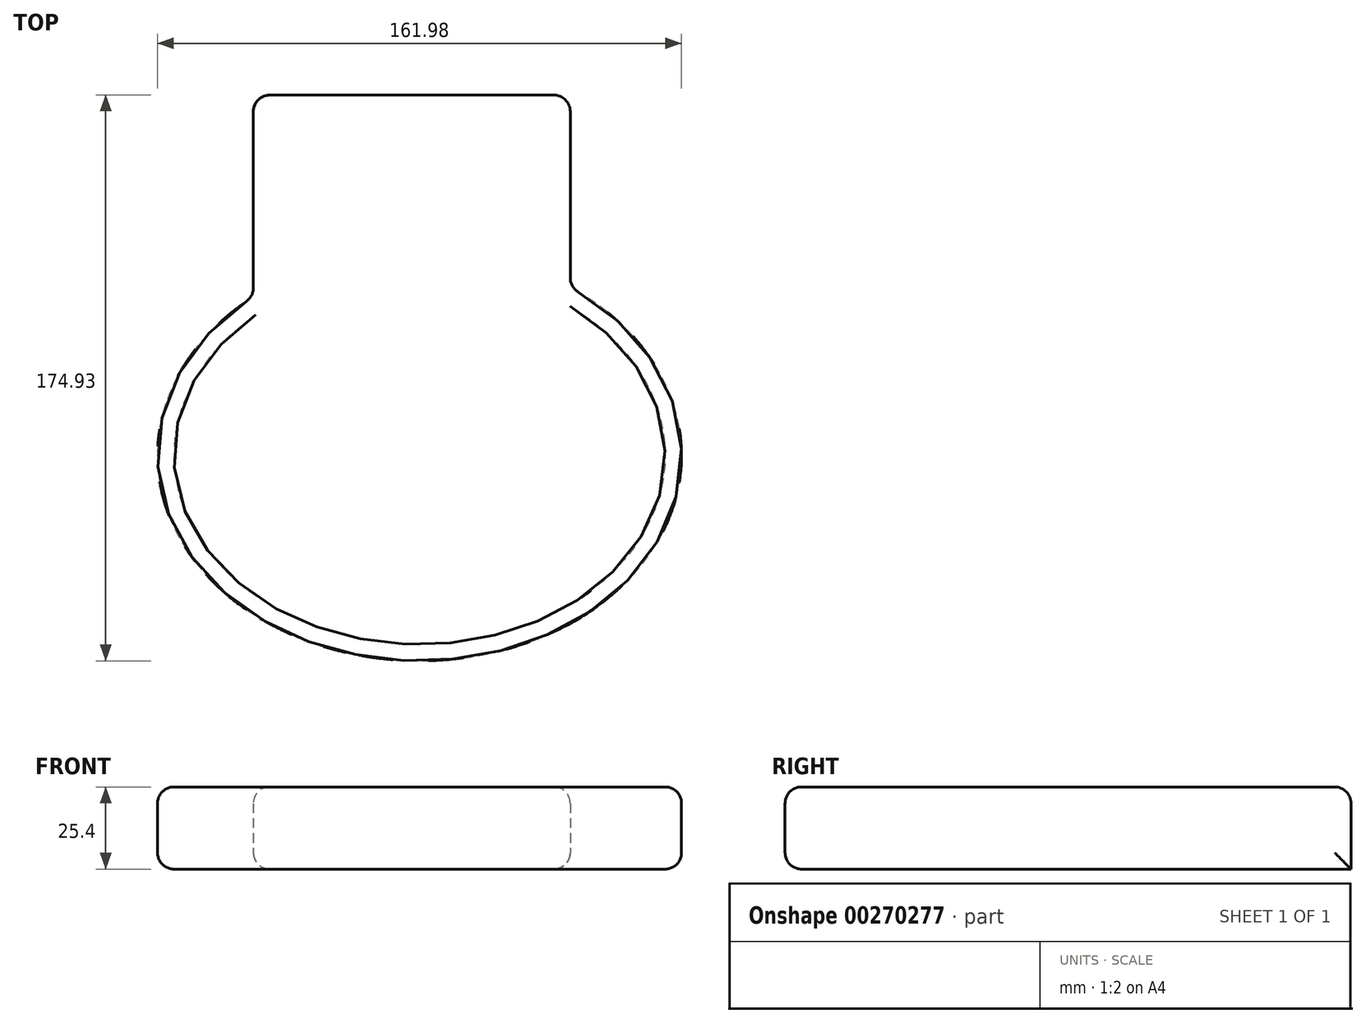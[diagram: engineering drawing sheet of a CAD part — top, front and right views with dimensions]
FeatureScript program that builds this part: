
annotation { "Feature Type Name" : "Feature", "Feature Type Description" : "" }
export const myFeature = defineFeature(function(context is Context, id is Id, definition is map)
    precondition{}
    {
        {
            var Q0;
            Q0=qCreatedBy(makeId("Top.planeOp"),FACE);
            var sketch = newSketch(context, id + "F0", { "sketchPlane" : qUnion([Q0])});
            skEllipse(sketch, "E0", {"center": v(0, 0) * mm, "majorRadius": 63.5 * mm, "minorRadius": 81 * mm, "majorAxis": v(0, 1)});
            skLineSegment(sketch, "E1", {"start": v(-51.38, 49.09) * mm, "end": v(-51.38, 111.43) * mm});
            skLineSegment(sketch, "E2", {"start": v(-51.38, 111.43) * mm, "end": v(46.59, 111.43) * mm});
            skLineSegment(sketch, "E3", {"start": v(46.59, 111.43) * mm, "end": v(46.59, 51.94) * mm});
            skSolve(sketch);
        }
        {
            var Q0;
            Q0 = qSketchRegion(id + "F0", true);
            var Q1;
            {var subQ0=sQuery(id+"F0.wireOp",EDGE,"E1");Q1=makeQuery(id+"F0.imprint","IMPRINT",FACE,{"disambiguationData":[TD([[makeQuery(id+"F0.imprint","IMPRINT",EDGE,{"derivedFrom":subQ0}),-1.0]])]});}
            extrude(context, id + "F1", {"entities" : qUnion([Q0, Q1]), "depth" : 25.4 * mm});
        }
        {
            var Q0;
            Q0=makeQuery(id+"F1.opExtrude","CAP_EDGE",EDGE,{"disambiguationData":[OSD([sQuery(id+"F0.wireOp",EDGE,"E0")])],"isStart":true});
            var Q1;
            Q1=makeQuery(id+"F1.opExtrude","CAP_EDGE",EDGE,{"disambiguationData":[OSD([sQuery(id+"F0.wireOp",EDGE,"E0")])],"isStart":false});
            var Q2;
            Q2=makeQuery(id+"F1.opExtrude","CAP_EDGE",EDGE,{"disambiguationData":[OSD([sQuery(id+"F0.wireOp",EDGE,"E3")])],"isStart":true});
            var Q3;
            Q3=makeQuery(id+"F1.opExtrude","CAP_EDGE",EDGE,{"disambiguationData":[OSD([sQuery(id+"F0.wireOp",EDGE,"E2")])],"isStart":false});
            var Q4;
            Q4=makeQuery(id+"F1.opExtrude","SWEPT_EDGE",EDGE,{"disambiguationData":[OSD([sQuery(id+"F0.wireOp",EDGE,"E2"),sQuery(id+"F0.wireOp",EDGE,"E3")])]});
            var Q5;
            Q5=makeQuery(id+"F1.opExtrude","CAP_EDGE",EDGE,{"disambiguationData":[OSD([sQuery(id+"F0.wireOp",EDGE,"E1")])],"isStart":false});
            var Q6;
            Q6=makeQuery(id+"F1.opExtrude","CAP_EDGE",EDGE,{"disambiguationData":[OSD([sQuery(id+"F0.wireOp",EDGE,"E3")])],"isStart":false});
            var Q7;
            Q7=makeQuery(id+"F1.opExtrude","SWEPT_EDGE",EDGE,{"disambiguationData":[OSD([sQuery(id+"F0.wireOp",EDGE,"E0"),sQuery(id+"F0.wireOp",EDGE,"E1")])]});
            var Q8;
            Q8=makeQuery(id+"F1.opExtrude","CAP_EDGE",EDGE,{"disambiguationData":[OSD([sQuery(id+"F0.wireOp",EDGE,"E1")])],"isStart":true});
            var Q9;
            Q9=makeQuery(id+"F1.opExtrude","SWEPT_EDGE",EDGE,{"disambiguationData":[OSD([sQuery(id+"F0.wireOp",EDGE,"E1"),sQuery(id+"F0.wireOp",EDGE,"E2")])]});
            var Q10;
            Q10=makeQuery(id+"F1.opExtrude","SWEPT_EDGE",EDGE,{"disambiguationData":[OSD([sQuery(id+"F0.wireOp",EDGE,"E0"),sQuery(id+"F0.wireOp",EDGE,"E3")])]});
            fillet(context, id + "F2", {"entities" : qUnion([Q0, Q1, Q2, Q3, Q4, Q5, Q6, Q7, Q8, Q9, Q10]), "radius" : 5.08 * mm, "tangentPropagation" : true, "allowEdgeOverflow" : false});
        }
    });
